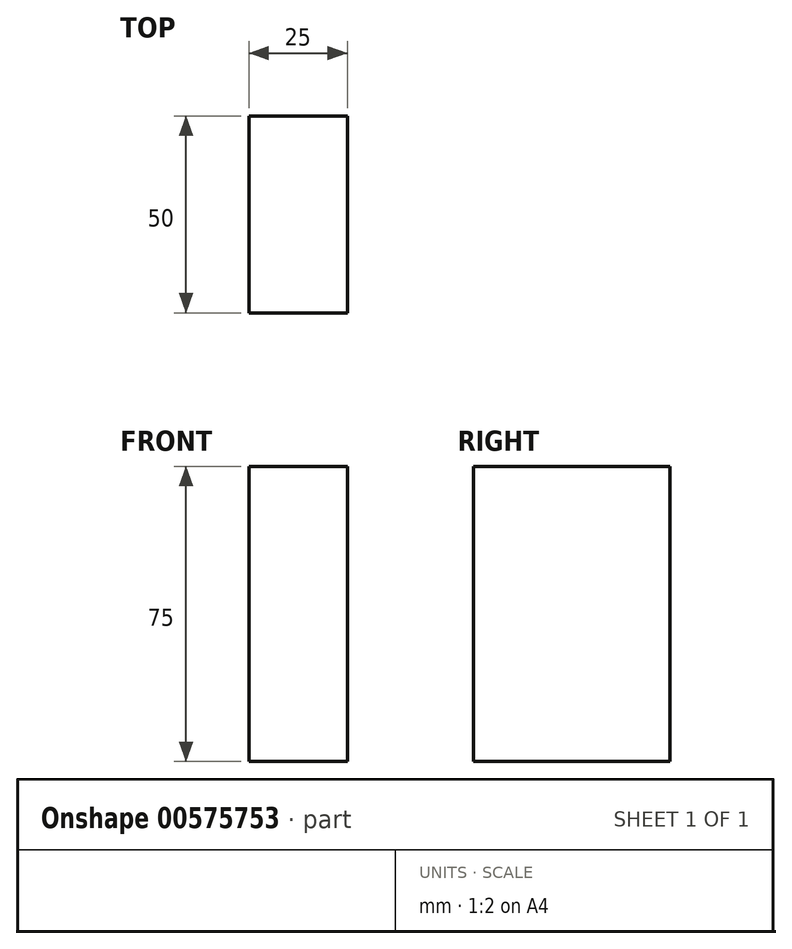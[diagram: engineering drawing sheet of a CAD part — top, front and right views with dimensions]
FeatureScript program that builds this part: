
annotation { "Feature Type Name" : "Feature", "Feature Type Description" : "" }
export const myFeature = defineFeature(function(context is Context, id is Id, definition is map)
    precondition{}
    {
        {
            var Q0;
            Q0=qCreatedBy(makeId("Top.planeOp"),FACE);
            var sketch = newSketch(context, id + "F0", { "sketchPlane" : qUnion([Q0])});
            skLineSegment(sketch, "E0.bottom", {"start": v(-55.68, 75.57) * mm, "end": v(-30.68, 75.57) * mm});
            skLineSegment(sketch, "E0.top", {"start": v(-55.68, 25.57) * mm, "end": v(-30.68, 25.57) * mm});
            skLineSegment(sketch, "E0.left", {"start": v(-55.68, 75.57) * mm, "end": v(-55.68, 25.57) * mm});
            skLineSegment(sketch, "E0.right", {"start": v(-30.68, 75.57) * mm, "end": v(-30.68, 25.57) * mm});
            skSolve(sketch);
        }
        {
            var Q0;
            Q0=makeQuery(id+"F0.imprint","IMPRINT",FACE,{"disambiguationData":[TD([[makeQuery(id+"F0.imprint","IMPRINT",EDGE,{"derivedFrom":sQuery(id+"F0.wireOp",EDGE,"E0.bottom")}),-1.0]])]});
            extrude(context, id + "F1", {"entities" : qUnion([Q0]), "depth" : 75 * mm, "offsetDistance" : 25 * mm});
        }
    });
